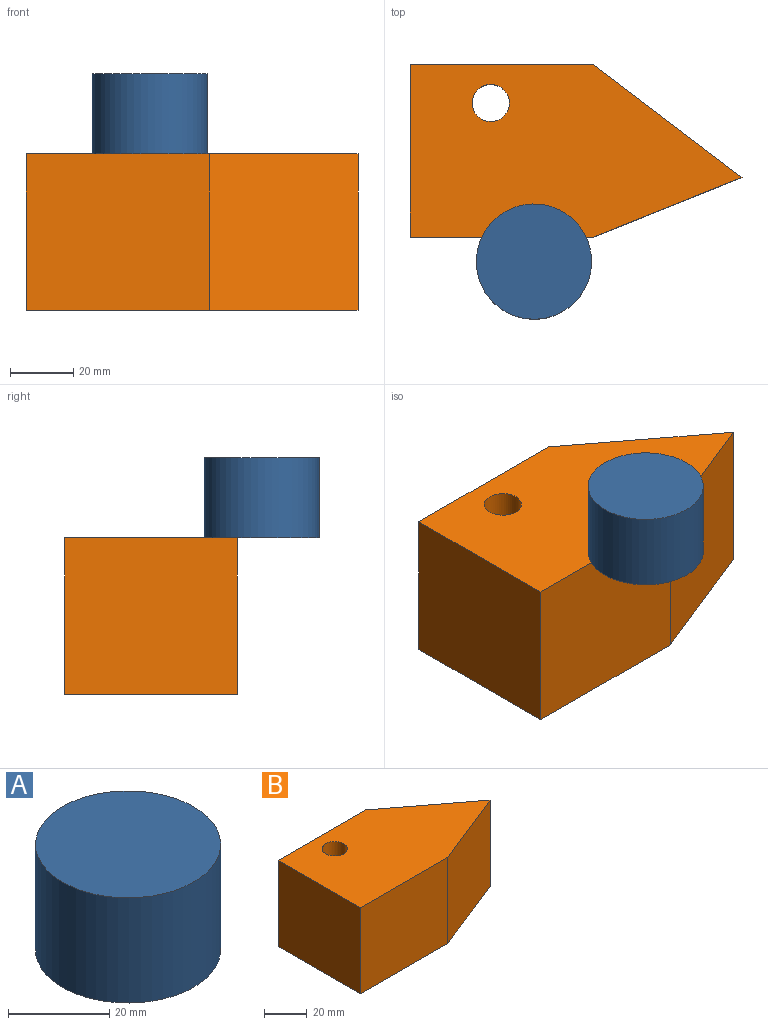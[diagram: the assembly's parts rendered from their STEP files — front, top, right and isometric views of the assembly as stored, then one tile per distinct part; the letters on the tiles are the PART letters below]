
ASSEMBLY  parts=2 mates=1
PART A: 3 faces, bbox 36.5x36.5x25.4 mm
  f0: cylinder r=18.26mm len=36.52mm, axis (0,0,-1), area 2914.5mm2, adj f1,f2
  f1: plane 36.52x36.52mm, normal (0,0,1), area 1047.7mm2, adj f0
  f2: plane 36.52x36.52mm, normal (0,0,-1), area 1047.7mm2, adj f0
PART B: 8 faces, bbox 105.2x54.6x49.5 mm
  f0: plane 54.62x49.53mm, normal (-1,0,0), area 2705.5mm2, adj f1,f4,f5,f6
  f1: plane 58.11x49.53mm, normal (0,-1,0), area 2878mm2, adj f0,f2,f5,f6
  f2: plane 49.53x47.11mm, normal (0.37,-0.93,0), area 2513.7mm2, adj f1,f3,f5,f6
  f3: plane 49.53x47.11mm, normal (0.6,0.8,0), area 2928.9mm2, adj f2,f4,f5,f6
  f4: plane 58.11x49.53mm, normal (0,1,0), area 2878mm2, adj f0,f3,f5,f6
  f5: plane 105.21x54.62mm, normal (0,0,1), area 4351.2mm2, adj f0,f1,f2,f3,f4,f7
  f6: plane 105.21x54.62mm, normal (0,0,-1), area 4351.2mm2, adj f0,f1,f2,f3,f4,f7
  f7: cylinder r=5.9mm len=49.53mm, axis (0,0,1), area 1835.5mm2, adj f5,f6
PLACE A t=(-78.65,-35.35,3.2)mm
PLACE B t=(-43.69,-79.74,-46.33)mm fixed
MATE planar B.f5 <-> A.f0  axis (0,0,1) through (-75.55,-33.02,3.2)mm
